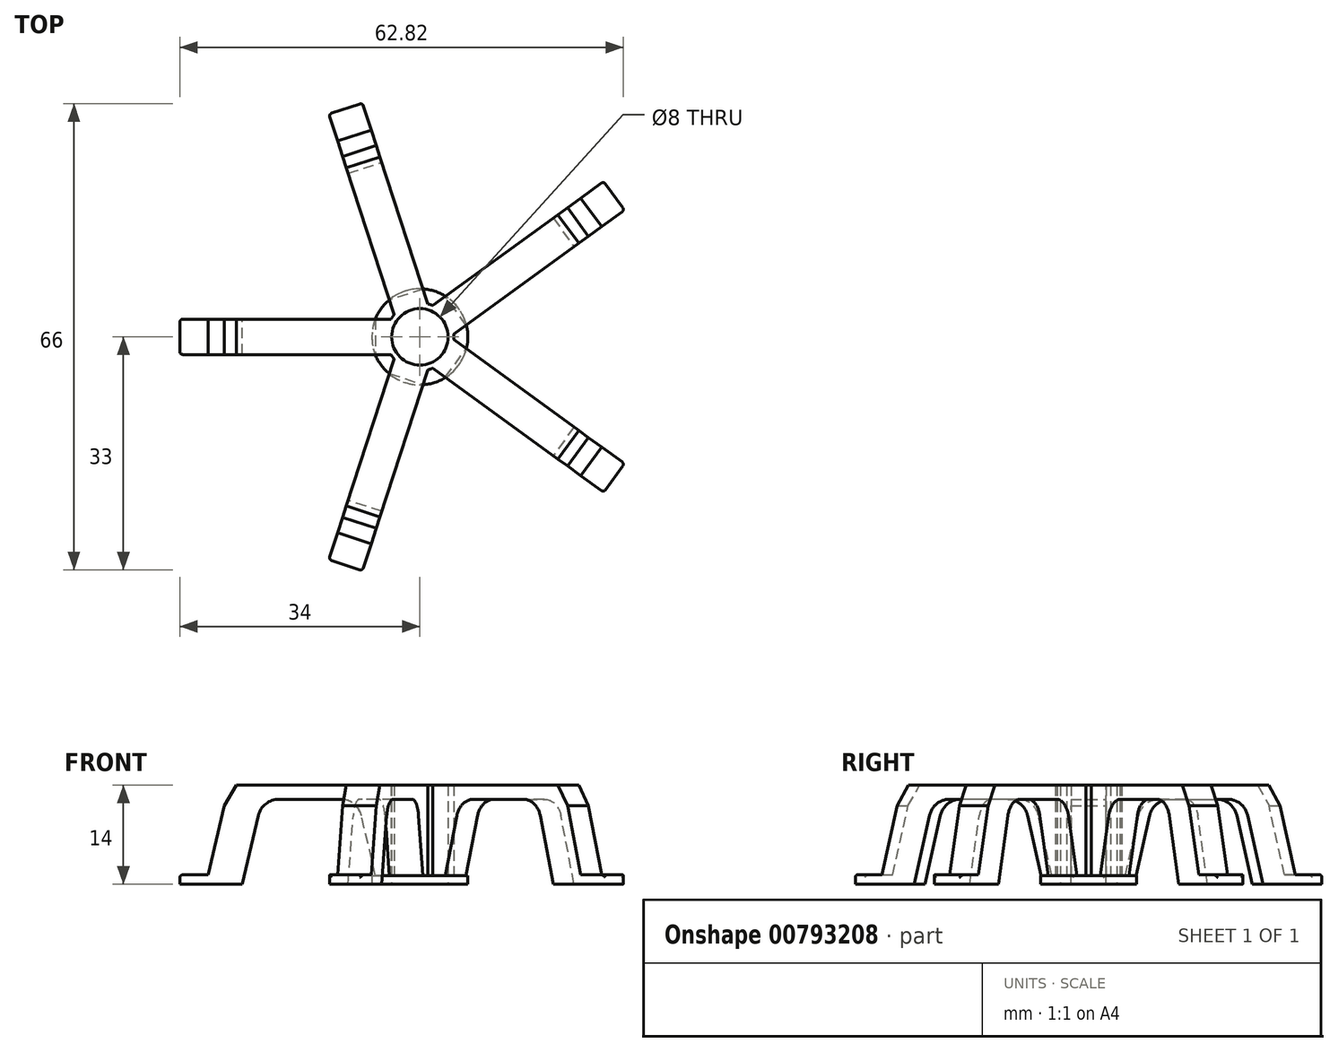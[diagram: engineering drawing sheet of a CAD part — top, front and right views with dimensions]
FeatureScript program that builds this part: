
annotation { "Feature Type Name" : "Feature", "Feature Type Description" : "" }
export const myFeature = defineFeature(function(context is Context, id is Id, definition is map)
    precondition{}
    {
        {
            var Q0;
            Q0=qCreatedBy(makeId("Top.planeOp"),FACE);
            var sketch = newSketch(context, id + "F0", { "sketchPlane" : qUnion([Q0])});
            skCircle(sketch, "E0", {"center": v(0, 0) * mm, "radius": 4 * mm});
            skCircle(sketch, "E1", {"center": v(0, 0) * mm, "radius": 30 * mm});
            skCircle(sketch, "E2.0", {"center": v(0, 0) * mm, "radius": 4.8 * mm});
            skCircle(sketch, "E3.0", {"center": v(0, 0) * mm, "radius": 6.8 * mm});
            skSolve(sketch);
        }
        {
            var Q0;
            Q0=makeQuery(id+"F0.imprint","IMPRINT",FACE,{"disambiguationData":[TD([[makeQuery(id+"F0.imprint","IMPRINT",EDGE,{"derivedFrom":sQuery(id+"F0.wireOp",EDGE,"E0")}),-1.0]])]});
            extrude(context, id + "F1", {"entities" : qUnion([Q0]), "depth" : 14 * mm, "offsetDistance" : 25 * mm});
        }
        {
            var Q0;
            Q0=makeQuery(id+"F0.imprint","IMPRINT",FACE,{"disambiguationData":[TD([[makeQuery(id+"F0.imprint","IMPRINT",EDGE,{"derivedFrom":sQuery(id+"F0.wireOp",EDGE,"E2.0")}),-1.0]])]});
            var Q1;
            Q1=sQuery(id+"F0.wireOp",EDGE,"E3.0");
            extrude(context, id + "F2", {"entities" : qUnion([Q0]), "surfaceEntities" : qUnion([Q1]), "depth" : 1.2 * mm, "offsetDistance" : 25 * mm});
        }
        {
            var Q0;
            Q0=qCreatedBy(makeId("Front.planeOp"),FACE);
            var sketch = newSketch(context, id + "F3", { "sketchPlane" : qUnion([Q0])});
            skLineSegment(sketch, "E4.0.0", {"start": v(-30, 0) * mm, "end": v(30, 0) * mm, "construction": true});
            skLineSegment(sketch, "E5", {"start": v(-30, 1.3) * mm, "end": v(-27, 14) * mm});
            skLineSegment(sketch, "E6", {"start": v(0, -7.84) * mm, "end": v(0, 20.86) * mm, "construction": true});
            skLineSegment(sketch, "E7", {"start": v(-4, 0) * mm, "end": v(-4, 14) * mm});
            skPoint(sketch, "E8", {"position": v(0, 0) * mm});
            skLineSegment(sketch, "E9", {"start": v(-34, 0) * mm, "end": v(-34, 1.3) * mm});
            skLineSegment(sketch, "E10", {"start": v(-34, 1.3) * mm, "end": v(-30, 1.3) * mm});
            skLineSegment(sketch, "E11", {"start": v(-4, 0) * mm, "end": v(-6, 0) * mm});
            skLineSegment(sketch, "E12", {"start": v(-6, 0) * mm, "end": v(-8.83, 12) * mm});
            skLineSegment(sketch, "E13", {"start": v(-8.83, 12) * mm, "end": v(-22.33, 12) * mm});
            skLineSegment(sketch, "E14", {"start": v(-4, 14) * mm, "end": v(-27, 14) * mm});
            skLineSegment(sketch, "E15.0", {"start": v(-4.8, 14) * mm, "end": v(4.8, 14) * mm});
            skLineSegment(sketch, "E16", {"start": v(-34, 0) * mm, "end": v(-25.17, 0) * mm});
            skLineSegment(sketch, "E17", {"start": v(-25.17, 0) * mm, "end": v(-22.33, 12) * mm});
            skSolve(sketch);
        }
        {
            var Q0;
            Q0 = qSketchRegion(id + "F3", true);
            extrude(context, id + "F4", {"entities" : qUnion([Q0]), "endBound" : BoundingType.SYMMETRIC, "depth" : 5 * mm, "offsetDistance" : 25 * mm});
        }
        {
            var Q0;
            Q0=makeQuery(id+"F4.opExtrude","CAP_EDGE",EDGE,{"disambiguationData":[OSD([sQuery(id+"F3.wireOp",EDGE,"E9")])],"isStart":false});
            var Q1;
            Q1=makeQuery(id+"F4.opExtrude","CAP_EDGE",EDGE,{"disambiguationData":[OSD([sQuery(id+"F3.wireOp",EDGE,"E9")])],"isStart":true});
            var Q2;
            Q2=makeQuery(id+"F4.opExtrude","SWEPT_EDGE",EDGE,{"disambiguationData":[OSD([sQuery(id+"F3.wireOp",EDGE,"E9"),sQuery(id+"F3.wireOp",EDGE,"E10")])]});
            fillet(context, id + "F5", {"entities" : qUnion([Q0, Q1, Q2]), "radius" : 0.4 * mm, "tangentPropagation" : true, "allowEdgeOverflow" : false});
        }
        {
            var Q0;
            Q0=makeQuery(id+"F4.opExtrude","SWEPT_EDGE",EDGE,{"disambiguationData":[OSD([sQuery(id+"F3.wireOp",EDGE,"E13"),sQuery(id+"F3.wireOp",EDGE,"E17")])]});
            var Q1;
            Q1=makeQuery(id+"F4.opExtrude","SWEPT_EDGE",EDGE,{"disambiguationData":[OSD([sQuery(id+"F3.wireOp",EDGE,"E12"),sQuery(id+"F3.wireOp",EDGE,"E13")])]});
            var Q2;
            Q2=makeQuery(id+"F8.opPattern","COPY",EDGE,{"derivedFrom":makeQuery(id+"F4.opExtrude","SWEPT_EDGE",EDGE,{"disambiguationData":[OSD([sQuery(id+"F3.wireOp",EDGE,"E12"),sQuery(id+"F3.wireOp",EDGE,"E13")])]}),"instanceName":"1"});
            var Q3;
            Q3=makeQuery(id+"F8.opPattern","COPY",EDGE,{"derivedFrom":makeQuery(id+"F4.opExtrude","SWEPT_EDGE",EDGE,{"disambiguationData":[OSD([sQuery(id+"F3.wireOp",EDGE,"E13"),sQuery(id+"F3.wireOp",EDGE,"E17")])]}),"instanceName":"1"});
            fillet(context, id + "F6", {"entities" : qUnion([Q0, Q1, Q2, Q3]), "radius" : 3 * mm, "tangentPropagation" : true, "allowEdgeOverflow" : false});
        }
        {
            var Q0;
            Q0=makeQuery(id+"F4.opExtrude","SWEPT_EDGE",EDGE,{"disambiguationData":[OSD([sQuery(id+"F3.wireOp",EDGE,"E5"),sQuery(id+"F3.wireOp",EDGE,"E14")])]});
            chamfer(context, id + "F7", {"entities" : qUnion([Q0]), "chamferType" : ChamferType.OFFSET_ANGLE, "width" : 1 * mm, "oppositeDirection" : true, "angle" : 60 * degree, "tangentPropagation" : true});
        }
        {
            var Q0;
            Q0=makeQuery(id+"F4.opExtrude","SWEPT_BODY",BODY,{"disambiguationData":[OSD([sQuery(id+"F3.wireOp",EDGE,"MgkDqmcN-hi2n-GAPe-Pphh-hkN7flm2gbDW"),sQuery(id+"F3.wireOp",EDGE,"ovK46Krt-dExm-RRu1-TiYX-nbYC2HejLqaH"),sQuery(id+"F3.wireOp",EDGE,"NXYB8RrR-Vrhu-Yukl-lUS1-GhXHnKy6lI7N"),sQuery(id+"F3.wireOp",EDGE,"E5"),sQuery(id+"F3.wireOp",EDGE,"P760gqC5-iCEU-fZj9-8pUp-ZUI3icDvE5JQ"),sQuery(id+"F3.wireOp",EDGE,"5xKDw0oW-jR8J-fbJE-42wB-ApoaM0ucCnCA"),sQuery(id+"F3.wireOp",EDGE,"P33ufyIM-T1RT-dyT6-9Abq-XaTNAI1OlTnU"),sQuery(id+"F3.wireOp",EDGE,"Es8br8GN-xfa7-4NFv-DxDh-1xmETvIxzcN5"),sQuery(id+"F3.wireOp",EDGE,"IknB6isL-mrQM-kcXy-nPub-CNLMJKXLFmgc"),sQuery(id+"F3.wireOp",EDGE,"2G3DJL60-d0dB-Bzsu-MyGW-rLJkTMlZKXYS"),sQuery(id+"F3.wireOp",EDGE,"E7")])]});
            var Q1;
            Q1=sQuery(id+"F3.wireOp",EDGE,"E6");
            circularPattern(context, id + "F8", {"operationType" : NewBodyOperationType.ADD, "entities" : qUnion([Q0]), "axis" : qUnion([Q1]), "angle" : 360 * degree, "instanceCount" : 5, "equalSpace" : true});
        }
    });
